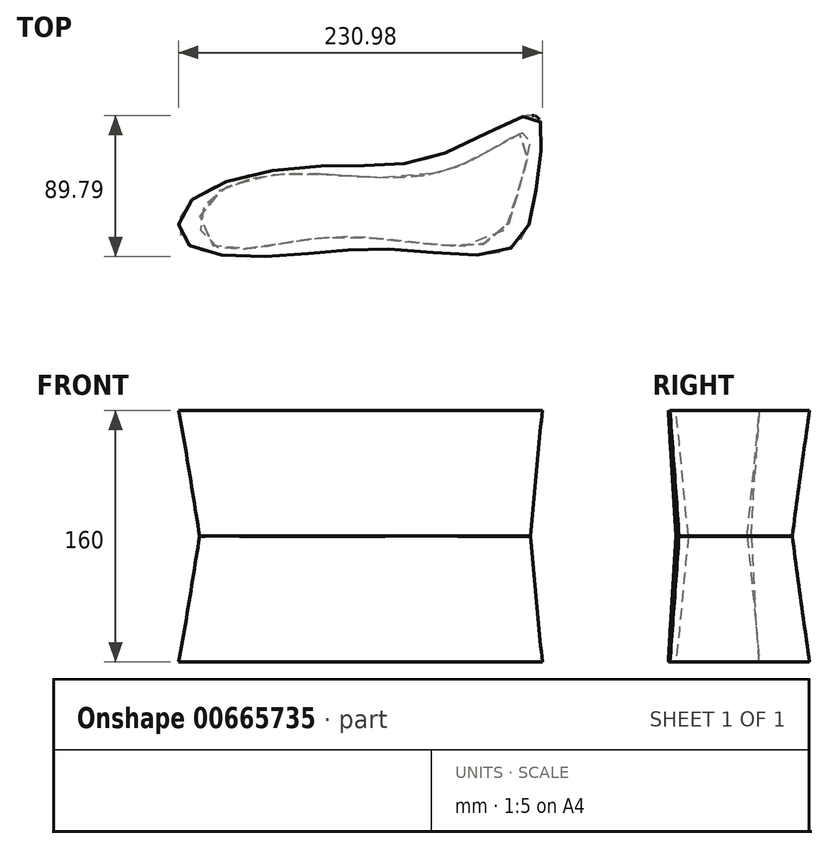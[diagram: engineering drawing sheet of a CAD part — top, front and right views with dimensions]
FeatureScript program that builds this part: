
annotation { "Feature Type Name" : "Feature", "Feature Type Description" : "" }
export const myFeature = defineFeature(function(context is Context, id is Id, definition is map)
    precondition{}
    {
        {
            var Q0;
            Q0=qCreatedBy(makeId("Top.planeOp"),FACE);
            var sketch = newSketch(context, id + "F0", { "sketchPlane" : qUnion([Q0])});
            skFitSpline(sketch, "E0", {"points": [v(-28.84, 31.5) * mm, v(-111.96, 9.02) * mm, v(-115.5, -16.42) * mm, v(-51.91, -25.3) * mm, v(21.15, -21.45) * mm, v(93.32, -19.67) * mm, v(109, 27.07) * mm, v(107.52, 63.15) * mm, v(47.48, 38.9) * mm, v(-28.84, 31.5) * mm]});
            skSolve(sketch);
        }
        {
            var Q0;
            Q0=qCreatedBy(makeId("Top.planeOp"),FACE);
            cPlane(context, id + "F1", {"entities" : qUnion([Q0]), "cplaneType" : CPlaneType.OFFSET, "offset" : 80 * mm, "width" : 150 * mm, "height" : 150 * mm});
        }
        {
            var Q0;
            Q0=qCreatedBy(id+"F1.planeOp",FACE);
            var sketch = newSketch(context, id + "F2", { "sketchPlane" : qUnion([Q0])});
            skFitSpline(sketch, "E1", {"points": [v(-12.57, 25.3) * mm, v(-68.18, 24.7) * mm, v(-103.68, 5.47) * mm, v(-100.13, -17.3) * mm, v(-55.17, -17.9) * mm, v(0, -13.75) * mm, v(80.01, -16.12) * mm, v(96.28, 15.23) * mm, v(102.79, 52.2) * mm, v(59.6, 31.8) * mm, v(-12.57, 25.3) * mm]});
            skSolve(sketch);
        }
        {
            var Q0;
            Q0=makeQuery(id+"F0.imprint","IMPRINT",FACE,{"disambiguationData":[TD([[makeQuery(id+"F0.imprint","IMPRINT",EDGE,{"derivedFrom":sQuery(id+"F0.wireOp",EDGE,"E0")}),1.0]])]});
            var Q1;
            Q1=makeQuery(id+"F2.imprint","IMPRINT",FACE,{"disambiguationData":[TD([[makeQuery(id+"F2.imprint","IMPRINT",EDGE,{"derivedFrom":sQuery(id+"F2.wireOp",EDGE,"E1")}),1.0]])]});
            loft(context, id + "F3", {"sheetProfilesArray" : [{ "sheetProfileEntities" : qUnion([Q0]) }, { "sheetProfileEntities" : qUnion([Q1]) }]});
        }
        {
            var Q0;
            Q0=makeQuery(id+"F3.opLoft","SWEPT_BODY",BODY,{"disambiguationData":[OSD([makeQuery(id+"F0.imprint","IMPRINT",FACE,{"disambiguationData":[TD([[makeQuery(id+"F0.imprint","IMPRINT",EDGE,{"derivedFrom":sQuery(id+"F0.wireOp",EDGE,"E0")}),1.0]])]}),makeQuery(id+"F2.imprint","IMPRINT",FACE,{"disambiguationData":[TD([[makeQuery(id+"F2.imprint","IMPRINT",EDGE,{"derivedFrom":sQuery(id+"F2.wireOp",EDGE,"E1")}),1.0]])]})])]});
            var Q1;
            Q1=qCreatedBy(id+"F1.planeOp",FACE);
            mirror(context, id + "F4", {"operationType" : NewBodyOperationType.ADD, "entities" : qUnion([Q0]), "mirrorPlane" : qUnion([Q1])});
        }
        {
            var Q0;
            {var subQ0=makeQuery(id+"F3.opLoft","MID_CAP_EDGE",EDGE,{"disambiguationData":[OSD([sQuery(id+"F0.wireOp",EDGE,"E0"),sQuery(id+"F2.wireOp",EDGE,"E1")])],"capPos":1.0});Q0=makeQuery(id+"F4.boolean.opBoolean","MERGE",EDGE,{"derivedFrom":[subQ0,makeQuery(id+"F4.opPattern","COPY",EDGE,{"derivedFrom":subQ0,"instanceName":"1"})]});}
            fillet(context, id + "F5", {"entities" : qUnion([Q0]), "radius" : 0.1 * mm, "tangentPropagation" : true, "allowEdgeOverflow" : false});
        }
    });
